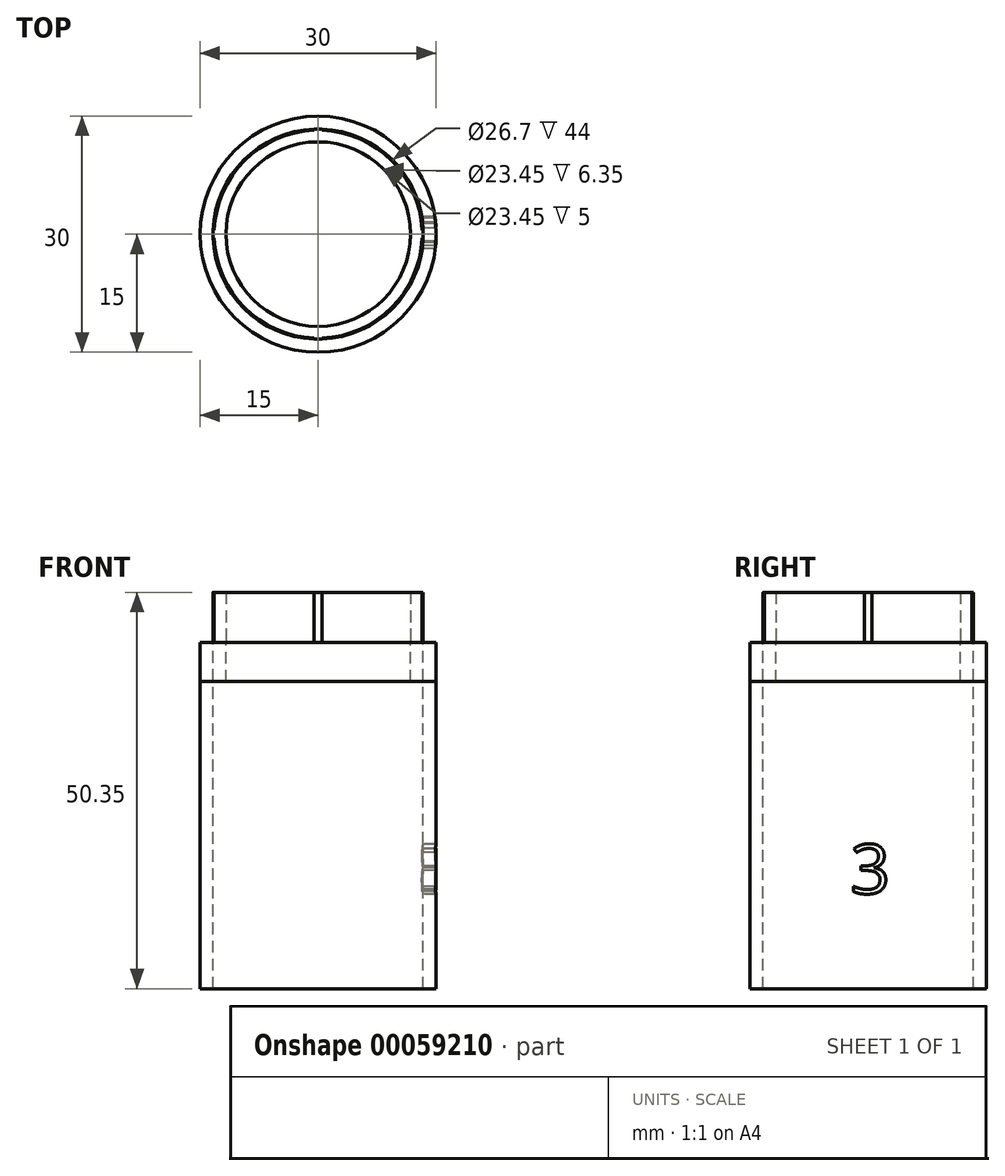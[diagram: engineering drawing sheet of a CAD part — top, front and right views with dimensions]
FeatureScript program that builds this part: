
annotation { "Feature Type Name" : "Feature", "Feature Type Description" : "" }
export const myFeature = defineFeature(function(context is Context, id is Id, definition is map)
    precondition{}
    {
        {
            var Q0;
            Q0=qCreatedBy(makeId("Top.planeOp"),FACE);
            var sketch = newSketch(context, id + "F0", { "sketchPlane" : qUnion([Q0])});
            skCircle(sketch, "E0", {"center": v(0, 0) * mm, "radius": 11.72 * mm});
            skCircle(sketch, "E1", {"center": v(0, 0) * mm, "radius": 13.2 * mm});
            skArc(sketch, "E2", {"start": v(13.34, -0.5) * mm, "mid": v(13.35, 0) * mm, "end": v(13.34, 0.5) * mm});
            skLineSegment(sketch, "E3", {"start": v(13.34, -0.5) * mm, "end": v(13.34, 0) * mm, "construction": true});
            skLineSegment(sketch, "E4", {"start": v(13.34, 0.5) * mm, "end": v(13.34, 0) * mm, "construction": true});
            skLineSegment(sketch, "E5", {"start": v(13.34, 0.5) * mm, "end": v(13.2, 0.5) * mm});
            skLineSegment(sketch, "E6", {"start": v(13.34, -0.5) * mm, "end": v(13.2, -0.5) * mm});
            skArc(sketch, "E7", {"start": v(0.5, 13.34) * mm, "mid": v(0, 13.35) * mm, "end": v(-0.5, 13.34) * mm});
            skLineSegment(sketch, "E8", {"start": v(-0.5, 13.34) * mm, "end": v(0, 13.34) * mm, "construction": true});
            skLineSegment(sketch, "E9", {"start": v(0.5, 13.34) * mm, "end": v(0, 13.34) * mm, "construction": true});
            skLineSegment(sketch, "E10", {"start": v(13.2, 0.5) * mm, "end": v(13.2, 0) * mm, "construction": true});
            skLineSegment(sketch, "E11", {"start": v(0.5, 13.34) * mm, "end": v(0.5, 13.2) * mm});
            skLineSegment(sketch, "E12", {"start": v(-0.5, 13.34) * mm, "end": v(-0.5, 13.2) * mm});
            skArc(sketch, "E13", {"start": v(-13.34, 0.5) * mm, "mid": v(-13.35, 0) * mm, "end": v(-13.34, -0.5) * mm});
            skLineSegment(sketch, "E14", {"start": v(-13.34, 0.5) * mm, "end": v(-13.34, 0) * mm, "construction": true});
            skLineSegment(sketch, "E15", {"start": v(-13.34, 0) * mm, "end": v(-13.34, -0.5) * mm, "construction": true});
            skLineSegment(sketch, "E16", {"start": v(-13.34, 0.5) * mm, "end": v(-13.2, 0.5) * mm});
            skLineSegment(sketch, "E17", {"start": v(-13.34, -0.5) * mm, "end": v(-13.2, -0.5) * mm});
            skArc(sketch, "E18", {"start": v(-0.5, -13.34) * mm, "mid": v(0, -13.35) * mm, "end": v(0.5, -13.34) * mm});
            skLineSegment(sketch, "E19", {"start": v(0.5, -13.34) * mm, "end": v(0, -13.34) * mm, "construction": true});
            skLineSegment(sketch, "E20", {"start": v(0, -13.34) * mm, "end": v(-0.5, -13.34) * mm, "construction": true});
            skLineSegment(sketch, "E21", {"start": v(0.5, -13.34) * mm, "end": v(0.5, -13.2) * mm});
            skLineSegment(sketch, "E22", {"start": v(-0.5, -13.34) * mm, "end": v(-0.5, -13.2) * mm});
            skSolve(sketch);
        }
        {
            var Q0;
            Q0=qSketchRegion(id+"F0",true);
            extrude(context, id + "F1", {"entities" : qUnion([Q0]), "depth" : 6.35 * mm});
        }
        {
            var Q0;
            Q0=qCreatedBy(makeId("Top.planeOp"),FACE);
            var sketch = newSketch(context, id + "F2", { "sketchPlane" : qUnion([Q0])});
            skCircle(sketch, "E23", {"center": v(0, 0) * mm, "radius": 13.35 * mm});
            skCircle(sketch, "E24", {"center": v(0, 0) * mm, "radius": 15 * mm});
            skSolve(sketch);
        }
        {
            var Q0;
            Q0=qSketchRegion(id+"F2",true);
            extrude(context, id + "F3", {"entities" : qUnion([Q0]), "operationType" : NewBodyOperationType.ADD, "oppositeDirection" : true, "depth" : 44 * mm});
        }
        {
            var Q0;
            Q0=qCreatedBy(makeId("Top.planeOp"),FACE);
            var sketch = newSketch(context, id + "F4", { "sketchPlane" : qUnion([Q0])});
            skCircle(sketch, "E25", {"center": v(0, 0) * mm, "radius": 11.72 * mm});
            skCircle(sketch, "E26", {"center": v(0, 0) * mm, "radius": 15 * mm});
            skSolve(sketch);
        }
        {
            var Q0;
            Q0=qSketchRegion(id+"F4",true);
            extrude(context, id + "F5", {"entities" : qUnion([Q0]), "oppositeDirection" : true, "depth" : 5 * mm});
        }
        {
            var Q0;
            Q0=qCreatedBy(makeId("Right.planeOp"),FACE);
            var sketch = newSketch(context, id + "F6", { "sketchPlane" : qUnion([Q0])});
            skText(sketch, "E27", { "text": "3\n", "fontName": "OpenSans-Regular.ttf"});
            const initialGuessF6  = {"E27": [-0.00224, -0.03192, 1, 0, 0.0063]};
            skSetInitialGuess(sketch, initialGuessF6);
            skSolve(sketch);
        }
        {
            var Q0;
            Q0=qSketchRegion(id+"F6",true);
            extrude(context, id + "F7", {"entities" : qUnion([Q0]), "operationType" : NewBodyOperationType.REMOVE, "depth" : 25 * mm});
        }
    });
